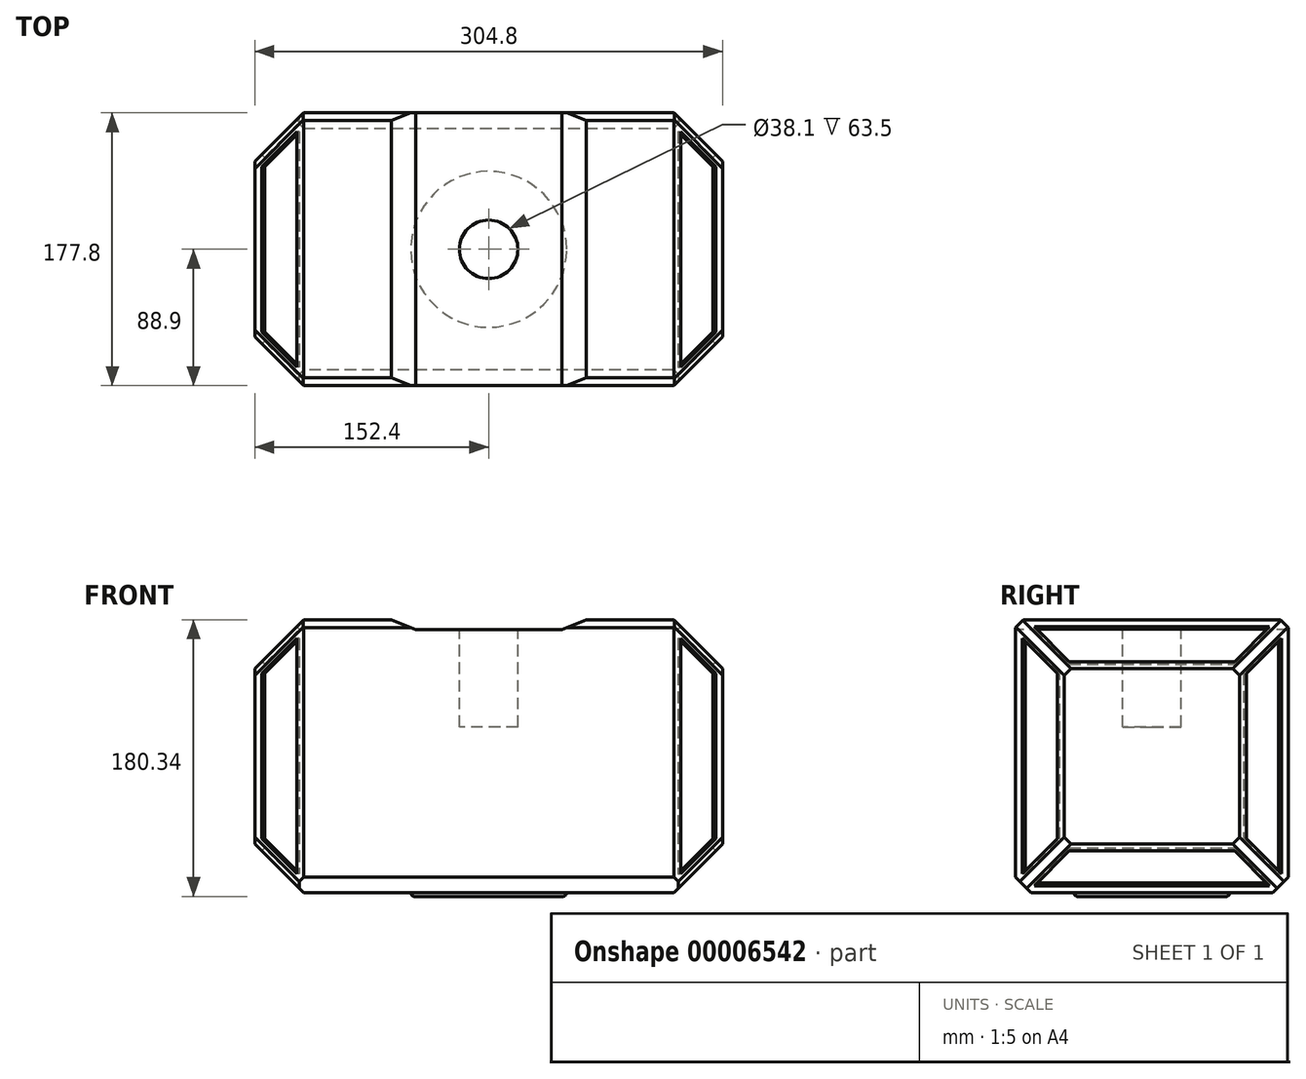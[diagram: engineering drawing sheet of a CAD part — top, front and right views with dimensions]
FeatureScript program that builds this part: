
annotation { "Feature Type Name" : "Feature", "Feature Type Description" : "" }
export const myFeature = defineFeature(function(context is Context, id is Id, definition is map)
    precondition{}
    {
        {
            var Q0;
            Q0=qCreatedBy(makeId("Top.planeOp"),FACE);
            var sketch = newSketch(context, id + "F0", { "sketchPlane" : qUnion([Q0])});
            skLineSegment(sketch, "E0.bottom", {"start": v(-152.4, -88.9) * mm, "end": v(152.4, -88.9) * mm});
            skLineSegment(sketch, "E0.top", {"start": v(-152.4, 88.9) * mm, "end": v(152.4, 88.9) * mm});
            skLineSegment(sketch, "E0.left", {"start": v(-152.4, -88.9) * mm, "end": v(-152.4, 88.9) * mm});
            skLineSegment(sketch, "E0.right", {"start": v(152.4, -88.9) * mm, "end": v(152.4, 88.9) * mm});
            skSolve(sketch);
        }
        {
            var Q0;
            Q0=makeQuery(id+"F0.imprint","IMPRINT",FACE,{"disambiguationData":[TD([[makeQuery(id+"F0.imprint","IMPRINT",EDGE,{"derivedFrom":sQuery(id+"F0.wireOp",EDGE,"E0.bottom")}),1.0]])]});
            extrude(context, id + "F1", {"entities" : qUnion([Q0]), "depth" : 177.8 * mm});
        }
        {
            var Q0;
            Q0=makeQuery(id+"F1.opExtrude","SWEPT_EDGE",EDGE,{"disambiguationData":[OSD([sQuery(id+"F0.wireOp",EDGE,"E0.bottom"),sQuery(id+"F0.wireOp",EDGE,"E0.left")])]});
            var Q1;
            Q1=makeQuery(id+"F1.opExtrude","CAP_EDGE",EDGE,{"disambiguationData":[OSD([sQuery(id+"F0.wireOp",EDGE,"E0.left")])],"isStart":false});
            var Q2;
            Q2=makeQuery(id+"F1.opExtrude","CAP_EDGE",EDGE,{"disambiguationData":[OSD([sQuery(id+"F0.wireOp",EDGE,"E0.left")])],"isStart":true});
            var Q3;
            Q3=makeQuery(id+"F1.opExtrude","SWEPT_EDGE",EDGE,{"disambiguationData":[OSD([sQuery(id+"F0.wireOp",EDGE,"E0.top"),sQuery(id+"F0.wireOp",EDGE,"E0.left")])]});
            var Q4;
            Q4=makeQuery(id+"F1.opExtrude","SWEPT_EDGE",EDGE,{"disambiguationData":[OSD([sQuery(id+"F0.wireOp",EDGE,"E0.bottom"),sQuery(id+"F0.wireOp",EDGE,"E0.right")])]});
            var Q5;
            Q5=makeQuery(id+"F1.opExtrude","CAP_EDGE",EDGE,{"disambiguationData":[OSD([sQuery(id+"F0.wireOp",EDGE,"E0.right")])],"isStart":false});
            var Q6;
            Q6=makeQuery(id+"F1.opExtrude","SWEPT_EDGE",EDGE,{"disambiguationData":[OSD([sQuery(id+"F0.wireOp",EDGE,"E0.top"),sQuery(id+"F0.wireOp",EDGE,"E0.right")])]});
            var Q7;
            Q7=makeQuery(id+"F1.opExtrude","CAP_EDGE",EDGE,{"disambiguationData":[OSD([sQuery(id+"F0.wireOp",EDGE,"E0.right")])],"isStart":true});
            chamfer(context, id + "F2", {"entities" : qUnion([Q0, Q1, Q2, Q3, Q4, Q5, Q6, Q7]), "width" : 31.75 * mm, "tangentPropagation" : true});
        }
        {
            var Q0;
            Q0=makeQuery(id+"F1.opExtrude","CAP_FACE",FACE,{"disambiguationData":[OSD([sQuery(id+"F0.wireOp",EDGE,"E0.bottom"),sQuery(id+"F0.wireOp",EDGE,"E0.top"),sQuery(id+"F0.wireOp",EDGE,"E0.left"),sQuery(id+"F0.wireOp",EDGE,"E0.right")])],"isStart":true});
            var sketch = newSketch(context, id + "F3", { "sketchPlane" : qUnion([Q0])});
            skCircle(sketch, "E1", {"center": v(0, 0) * mm, "radius": 50.8 * mm});
            skSolve(sketch);
        }
        {
            var Q0;
            Q0=makeQuery(id+"F3.imprint","IMPRINT",FACE,{"disambiguationData":[TD([[makeQuery(id+"F3.imprint","IMPRINT",EDGE,{"derivedFrom":sQuery(id+"F3.wireOp",EDGE,"E1")}),1.0]])]});
            extrude(context, id + "F4", {"entities" : qUnion([Q0]), "operationType" : NewBodyOperationType.ADD, "depth" : 2.54 * mm});
        }
        {
            var Q0;
            Q0=makeQuery(id+"F4.opExtrude","CAP_EDGE",EDGE,{"disambiguationData":[OSD([sQuery(id+"F3.wireOp",EDGE,"E1")])],"isStart":false});
            fillet(context, id + "F5", {"entities" : qUnion([Q0]), "radius" : 2.54 * mm, "tangentPropagation" : true, "allowEdgeOverflow" : false});
        }
        {
            var Q0;
            {var subQ0=sQuery(id+"F0.wireOp",EDGE,"E0.right");Q0=makeQuery(id+"F2.opChamfer","BLEND_FACE",FACE,{"disambiguationData":[OSD([subQ0]),TDD([makeQuery(id+"F1.opExtrude","CAP_EDGE",EDGE,{"disambiguationData":[OSD([subQ0])],"isStart":false})])]});}
            var sketch = newSketch(context, id + "F6", { "sketchPlane" : qUnion([Q0])});
            skLineSegment(sketch, "E2.0", {"start": v(53.86, 1.86) * mm, "end": v(76.63, 34.06) * mm});
            skLineSegment(sketch, "E2.1", {"start": v(53.86, 1.86) * mm, "end": v(-53.86, 1.86) * mm});
            skLineSegment(sketch, "E2.2", {"start": v(-76.63, 34.06) * mm, "end": v(-53.86, 1.86) * mm});
            skLineSegment(sketch, "E2.3", {"start": v(-76.63, 34.06) * mm, "end": v(76.63, 34.06) * mm});
            skSolve(sketch);
        }
        {
            var Q0;
            Q0=makeQuery(id+"F6.imprint","IMPRINT",FACE,{"disambiguationData":[TD([[makeQuery(id+"F6.imprint","IMPRINT",EDGE,{"derivedFrom":sQuery(id+"F6.wireOp",EDGE,"E2.0")}),1.0]])]});
            extrude(context, id + "F7", {"entities" : qUnion([Q0]), "operationType" : NewBodyOperationType.REMOVE, "oppositeDirection" : true, "depth" : 2.54 * mm});
        }
        {
            var Q0;
            Q0=qCreatedBy(makeId("Front.planeOp"),FACE);
            var sketch = newSketch(context, id + "F8", { "sketchPlane" : qUnion([Q0])});
            skLineSegment(sketch, "E3", {"start": v(0, 88.9) * mm, "end": v(232.88, 88.9) * mm});
            skSolve(sketch);
        }
        {
            var Q0;
            Q0=makeQuery(id+"F7.boolean.opBoolean","COPY",FACE,{"derivedFrom":makeQuery(id+"F7.opExtrude","CAP_FACE",FACE,{"disambiguationData":[OSD([sQuery(id+"F6.wireOp",EDGE,"E2.0"),sQuery(id+"F6.wireOp",EDGE,"E2.1"),sQuery(id+"F6.wireOp",EDGE,"E2.2"),sQuery(id+"F6.wireOp",EDGE,"E2.3")])],"isStart":false})});
            var Q1;
            Q1=makeQuery(id+"F7.boolean.opBoolean","COPY",FACE,{"derivedFrom":makeQuery(id+"F7.opExtrude","SWEPT_FACE",FACE,{"disambiguationData":[OSD([sQuery(id+"F6.wireOp",EDGE,"E2.0")])]})});
            var Q2;
            Q2=makeQuery(id+"F7.boolean.opBoolean","COPY",FACE,{"derivedFrom":makeQuery(id+"F7.opExtrude","SWEPT_FACE",FACE,{"disambiguationData":[OSD([sQuery(id+"F6.wireOp",EDGE,"E2.3")])]})});
            var Q3;
            Q3=makeQuery(id+"F7.boolean.opBoolean","COPY",FACE,{"derivedFrom":makeQuery(id+"F7.opExtrude","SWEPT_FACE",FACE,{"disambiguationData":[OSD([sQuery(id+"F6.wireOp",EDGE,"E2.1")])]})});
            var Q4;
            Q4=makeQuery(id+"F7.boolean.opBoolean","COPY",FACE,{"derivedFrom":makeQuery(id+"F7.opExtrude","SWEPT_FACE",FACE,{"disambiguationData":[OSD([sQuery(id+"F6.wireOp",EDGE,"E2.2")])]})});
            var Q5;
            Q5=sQuery(id+"F8.wireOp",EDGE,"E3");
            circularPattern(context, id + "F9", {"faces" : qUnion([Q0, Q1, Q2, Q3, Q4]), "axis" : qUnion([Q5]), "angle" : 90 * degree, "instanceCount" : 4, "patternType" : PatternType.FACE});
        }
        {
            var Q0;
            {var subQ0=sQuery(id+"F0.wireOp",EDGE,"E0.left");Q0=makeQuery(id+"F2.opChamfer","BLEND_FACE",FACE,{"disambiguationData":[OSD([subQ0]),TDD([makeQuery(id+"F1.opExtrude","CAP_EDGE",EDGE,{"disambiguationData":[OSD([subQ0])],"isStart":true})])]});}
            var sketch = newSketch(context, id + "F10", { "sketchPlane" : qUnion([Q0])});
            skLineSegment(sketch, "E4.0", {"start": v(53.86, 123.86) * mm, "end": v(76.63, 91.66) * mm});
            skLineSegment(sketch, "E4.1", {"start": v(-53.86, 123.86) * mm, "end": v(53.86, 123.86) * mm});
            skLineSegment(sketch, "E4.2", {"start": v(-76.63, 91.66) * mm, "end": v(-53.86, 123.86) * mm});
            skLineSegment(sketch, "E4.3", {"start": v(76.63, 91.66) * mm, "end": v(-76.63, 91.66) * mm});
            skSolve(sketch);
        }
        {
            var Q0;
            Q0=makeQuery(id+"F10.imprint","IMPRINT",FACE,{"disambiguationData":[TD([[makeQuery(id+"F10.imprint","IMPRINT",EDGE,{"derivedFrom":sQuery(id+"F10.wireOp",EDGE,"E4.0")}),-1.0]])]});
            extrude(context, id + "F11", {"entities" : qUnion([Q0]), "operationType" : NewBodyOperationType.REMOVE, "oppositeDirection" : true, "depth" : 2.54 * mm});
        }
        {
            var Q0;
            Q0=qCreatedBy(makeId("Front.planeOp"),FACE);
            var sketch = newSketch(context, id + "F12", { "sketchPlane" : qUnion([Q0])});
            skLineSegment(sketch, "E5", {"start": v(0, 88.9) * mm, "end": v(227.16, 88.9) * mm});
            skSolve(sketch);
        }
        {
            var Q0;
            Q0=makeQuery(id+"F11.boolean.opBoolean","COPY",FACE,{"derivedFrom":makeQuery(id+"F11.opExtrude","SWEPT_FACE",FACE,{"disambiguationData":[OSD([sQuery(id+"F10.wireOp",EDGE,"E4.3")])]})});
            var Q1;
            Q1=makeQuery(id+"F11.boolean.opBoolean","COPY",FACE,{"derivedFrom":makeQuery(id+"F11.opExtrude","SWEPT_FACE",FACE,{"disambiguationData":[OSD([sQuery(id+"F10.wireOp",EDGE,"E4.2")])]})});
            var Q2;
            Q2=makeQuery(id+"F11.boolean.opBoolean","COPY",FACE,{"derivedFrom":makeQuery(id+"F11.opExtrude","SWEPT_FACE",FACE,{"disambiguationData":[OSD([sQuery(id+"F10.wireOp",EDGE,"E4.0")])]})});
            var Q3;
            Q3=makeQuery(id+"F11.boolean.opBoolean","COPY",FACE,{"derivedFrom":makeQuery(id+"F11.opExtrude","SWEPT_FACE",FACE,{"disambiguationData":[OSD([sQuery(id+"F10.wireOp",EDGE,"E4.1")])]})});
            var Q4;
            Q4=makeQuery(id+"F11.boolean.opBoolean","COPY",FACE,{"derivedFrom":makeQuery(id+"F11.opExtrude","CAP_FACE",FACE,{"disambiguationData":[OSD([sQuery(id+"F10.wireOp",EDGE,"E4.0"),sQuery(id+"F10.wireOp",EDGE,"E4.1"),sQuery(id+"F10.wireOp",EDGE,"E4.2"),sQuery(id+"F10.wireOp",EDGE,"E4.3")])],"isStart":false})});
            var Q5;
            Q5=sQuery(id+"F12.wireOp",EDGE,"E5");
            circularPattern(context, id + "F13", {"faces" : qUnion([Q0, Q1, Q2, Q3, Q4]), "axis" : qUnion([Q5]), "angle" : 90 * degree, "instanceCount" : 4, "patternType" : PatternType.FACE});
        }
        {
            var Q0;
            Q0=makeQuery(id+"F1.opExtrude","SWEPT_FACE",FACE,{"disambiguationData":[OSD([sQuery(id+"F0.wireOp",EDGE,"E0.bottom")])]});
            var sketch = newSketch(context, id + "F14", { "sketchPlane" : qUnion([Q0])});
            skLineSegment(sketch, "E6", {"start": v(0, 177.8) * mm, "end": v(0, -20.13) * mm});
            skLineSegment(sketch, "E7", {"start": v(0, 171.45) * mm, "end": v(47.7, 171.45) * mm});
            skLineSegment(sketch, "E8", {"start": v(47.7, 171.45) * mm, "end": v(63.5, 177.8) * mm});
            skLineSegment(sketch, "E9.0.MirrorCS", {"start": v(0, 171.45) * mm, "end": v(-47.7, 171.45) * mm});
            skLineSegment(sketch, "E10.0.MirrorCS", {"start": v(-47.7, 171.45) * mm, "end": v(-63.5, 177.8) * mm});
            skSolve(sketch);
        }
        {
            var Q0;
            {var subQ4=sQuery(id+"F14.wireOp",EDGE,"E9.0.MirrorCS");Q0=makeQuery(id+"F14.imprint","IMPRINT",FACE,{"disambiguationData":[TD([[makeQuery(id+"F14.imprint","IMPRINT",EDGE,{"derivedFrom":subQ4}),-1.0]])]});}
            var Q1;
            {var subQ4=sQuery(id+"F14.wireOp",EDGE,"E7");Q1=makeQuery(id+"F14.imprint","IMPRINT",FACE,{"disambiguationData":[TD([[makeQuery(id+"F14.imprint","IMPRINT",EDGE,{"derivedFrom":subQ4}),1.0]])]});}
            extrude(context, id + "F15", {"entities" : qUnion([Q0, Q1]), "operationType" : NewBodyOperationType.REMOVE, "oppositeDirection" : true, "depth" : 177.8 * mm});
        }
        {
            var Q0;
            Q0=makeQuery(id+"F1.opExtrude","CAP_EDGE",EDGE,{"disambiguationData":[OSD([sQuery(id+"F0.wireOp",EDGE,"E0.bottom")])],"isStart":true});
            var Q1;
            Q1=makeQuery(id+"F1.opExtrude","CAP_EDGE",EDGE,{"disambiguationData":[OSD([sQuery(id+"F0.wireOp",EDGE,"E0.top")])],"isStart":true});
            chamfer(context, id + "F16", {"entities" : qUnion([Q0, Q1]), "width" : 10.16 * mm, "tangentPropagation" : true});
        }
        {
            var Q0;
            {var subQ0=sQuery(id+"F0.wireOp",EDGE,"E0.left");Q0=makeQuery(id+"F2.opChamfer","BLEND_EDGE",EDGE,{"blendedFrom":[makeQuery(id+"F1.opExtrude","SWEPT_EDGE",EDGE,{"disambiguationData":[OSD([sQuery(id+"F0.wireOp",EDGE,"E0.bottom"),subQ0])]}),makeQuery(id+"F1.opExtrude","CAP_EDGE",EDGE,{"disambiguationData":[OSD([subQ0])],"isStart":true})],"blendedInto":[]});}
            var Q1;
            {var subQ0=sQuery(id+"F0.wireOp",EDGE,"E0.left");Q1=makeQuery(id+"F2.opChamfer","BLEND_EDGE",EDGE,{"blendedFrom":[makeQuery(id+"F1.opExtrude","SWEPT_EDGE",EDGE,{"disambiguationData":[OSD([sQuery(id+"F0.wireOp",EDGE,"E0.top"),subQ0])]}),makeQuery(id+"F1.opExtrude","CAP_EDGE",EDGE,{"disambiguationData":[OSD([subQ0])],"isStart":true})],"blendedInto":[]});}
            var Q2;
            {var subQ0=sQuery(id+"F0.wireOp",EDGE,"E0.right");Q2=makeQuery(id+"F2.opChamfer","BLEND_EDGE",EDGE,{"blendedFrom":[makeQuery(id+"F1.opExtrude","SWEPT_EDGE",EDGE,{"disambiguationData":[OSD([sQuery(id+"F0.wireOp",EDGE,"E0.top"),subQ0])]}),makeQuery(id+"F1.opExtrude","CAP_EDGE",EDGE,{"disambiguationData":[OSD([subQ0])],"isStart":true})],"blendedInto":[]});}
            var Q3;
            {var subQ0=sQuery(id+"F0.wireOp",EDGE,"E0.right");Q3=makeQuery(id+"F2.opChamfer","BLEND_EDGE",EDGE,{"blendedFrom":[makeQuery(id+"F1.opExtrude","SWEPT_EDGE",EDGE,{"disambiguationData":[OSD([sQuery(id+"F0.wireOp",EDGE,"E0.bottom"),subQ0])]}),makeQuery(id+"F1.opExtrude","CAP_EDGE",EDGE,{"disambiguationData":[OSD([subQ0])],"isStart":true})],"blendedInto":[]});}
            var Q4;
            {var subQ0=sQuery(id+"F0.wireOp",EDGE,"E0.left");Q4=makeQuery(id+"F2.opChamfer","BLEND_EDGE",EDGE,{"blendedFrom":[makeQuery(id+"F1.opExtrude","SWEPT_EDGE",EDGE,{"disambiguationData":[OSD([sQuery(id+"F0.wireOp",EDGE,"E0.top"),subQ0])]}),makeQuery(id+"F1.opExtrude","CAP_EDGE",EDGE,{"disambiguationData":[OSD([subQ0])],"isStart":false})],"blendedInto":[]});}
            var Q5;
            {var subQ0=sQuery(id+"F0.wireOp",EDGE,"E0.left");Q5=makeQuery(id+"F2.opChamfer","BLEND_EDGE",EDGE,{"blendedFrom":[makeQuery(id+"F1.opExtrude","SWEPT_EDGE",EDGE,{"disambiguationData":[OSD([sQuery(id+"F0.wireOp",EDGE,"E0.bottom"),subQ0])]}),makeQuery(id+"F1.opExtrude","CAP_EDGE",EDGE,{"disambiguationData":[OSD([subQ0])],"isStart":false})],"blendedInto":[]});}
            var Q6;
            {var subQ0=sQuery(id+"F0.wireOp",EDGE,"E0.right");Q6=makeQuery(id+"F2.opChamfer","BLEND_EDGE",EDGE,{"blendedFrom":[makeQuery(id+"F1.opExtrude","SWEPT_EDGE",EDGE,{"disambiguationData":[OSD([sQuery(id+"F0.wireOp",EDGE,"E0.bottom"),subQ0])]}),makeQuery(id+"F1.opExtrude","CAP_EDGE",EDGE,{"disambiguationData":[OSD([subQ0])],"isStart":false})],"blendedInto":[]});}
            var Q7;
            {var subQ0=sQuery(id+"F0.wireOp",EDGE,"E0.right");Q7=makeQuery(id+"F2.opChamfer","BLEND_EDGE",EDGE,{"blendedFrom":[makeQuery(id+"F1.opExtrude","SWEPT_EDGE",EDGE,{"disambiguationData":[OSD([sQuery(id+"F0.wireOp",EDGE,"E0.top"),subQ0])]}),makeQuery(id+"F1.opExtrude","CAP_EDGE",EDGE,{"disambiguationData":[OSD([subQ0])],"isStart":false})],"blendedInto":[]});}
            chamfer(context, id + "F17", {"entities" : qUnion([Q0, Q1, Q2, Q3, Q4, Q5, Q6, Q7]), "width" : 6.35 * mm, "tangentPropagation" : true});
        }
        {
            var Q0;
            {var subQ0=sQuery(id+"F0.wireOp",EDGE,"E0.bottom");Q0=makeQuery(id+"F15.boolean.opBoolean","SPLIT",EDGE,{"disambiguationData":[TD([makeQuery(id+"F15.opExtrude","SWEPT_FACE",FACE,{"disambiguationData":[OSD([sQuery(id+"F14.wireOp",EDGE,"E10.0.MirrorCS")])]})])],"derivedFrom":makeQuery(id+"F1.opExtrude","CAP_EDGE",EDGE,{"disambiguationData":[OSD([subQ0])],"isStart":false})});}
            var Q1;
            Q1=makeQuery(id+"F15.boolean.opBoolean","COPY",EDGE,{"derivedFrom":makeQuery(id+"F15.opExtrude","CAP_EDGE",EDGE,{"disambiguationData":[OSD([sQuery(id+"F14.wireOp",EDGE,"E10.0.MirrorCS")])],"isStart":true})});
            var Q2;
            Q2=makeQuery(id+"F15.boolean.opBoolean","COPY",EDGE,{"derivedFrom":makeQuery(id+"F15.opExtrude","CAP_EDGE",EDGE,{"disambiguationData":[OSD([sQuery(id+"F14.wireOp",EDGE,"E7"),sQuery(id+"F14.wireOp",EDGE,"E9.0.MirrorCS")])],"isStart":true})});
            var Q3;
            Q3=makeQuery(id+"F15.boolean.opBoolean","COPY",EDGE,{"derivedFrom":makeQuery(id+"F15.opExtrude","CAP_EDGE",EDGE,{"disambiguationData":[OSD([sQuery(id+"F14.wireOp",EDGE,"E8")])],"isStart":true})});
            var Q4;
            {var subQ0=sQuery(id+"F0.wireOp",EDGE,"E0.bottom");Q4=makeQuery(id+"F15.boolean.opBoolean","SPLIT",EDGE,{"disambiguationData":[TD([makeQuery(id+"F15.opExtrude","SWEPT_FACE",FACE,{"disambiguationData":[OSD([sQuery(id+"F14.wireOp",EDGE,"E8")])]})])],"derivedFrom":makeQuery(id+"F1.opExtrude","CAP_EDGE",EDGE,{"disambiguationData":[OSD([subQ0])],"isStart":false})});}
            var Q5;
            {var subQ0=sQuery(id+"F0.wireOp",EDGE,"E0.top");Q5=makeQuery(id+"F15.boolean.opBoolean","SPLIT",EDGE,{"disambiguationData":[TD([makeQuery(id+"F15.opExtrude","SWEPT_FACE",FACE,{"disambiguationData":[OSD([sQuery(id+"F14.wireOp",EDGE,"E8")])]})])],"derivedFrom":makeQuery(id+"F1.opExtrude","CAP_EDGE",EDGE,{"disambiguationData":[OSD([subQ0])],"isStart":false})});}
            var Q6;
            Q6=makeQuery(id+"F15.boolean.opBoolean","COPY",EDGE,{"derivedFrom":makeQuery(id+"F15.opExtrude","CAP_EDGE",EDGE,{"disambiguationData":[OSD([sQuery(id+"F14.wireOp",EDGE,"E8")])],"isStart":false})});
            var Q7;
            Q7=makeQuery(id+"F15.boolean.opBoolean","COPY",EDGE,{"derivedFrom":makeQuery(id+"F15.opExtrude","CAP_EDGE",EDGE,{"disambiguationData":[OSD([sQuery(id+"F14.wireOp",EDGE,"E7"),sQuery(id+"F14.wireOp",EDGE,"E9.0.MirrorCS")])],"isStart":false})});
            var Q8;
            Q8=makeQuery(id+"F15.boolean.opBoolean","COPY",EDGE,{"derivedFrom":makeQuery(id+"F15.opExtrude","CAP_EDGE",EDGE,{"disambiguationData":[OSD([sQuery(id+"F14.wireOp",EDGE,"E10.0.MirrorCS")])],"isStart":false})});
            var Q9;
            {var subQ0=sQuery(id+"F0.wireOp",EDGE,"E0.top");Q9=makeQuery(id+"F15.boolean.opBoolean","SPLIT",EDGE,{"disambiguationData":[TD([makeQuery(id+"F15.opExtrude","SWEPT_FACE",FACE,{"disambiguationData":[OSD([sQuery(id+"F14.wireOp",EDGE,"E10.0.MirrorCS")])]})])],"derivedFrom":makeQuery(id+"F1.opExtrude","CAP_EDGE",EDGE,{"disambiguationData":[OSD([subQ0])],"isStart":false})});}
            chamfer(context, id + "F18", {"entities" : qUnion([Q0, Q1, Q2, Q3, Q4, Q5, Q6, Q7, Q8, Q9]), "width" : 5.08 * mm, "tangentPropagation" : true});
        }
        {
            var Q0;
            Q0=makeQuery(id+"F15.boolean.opBoolean","COPY",FACE,{"derivedFrom":makeQuery(id+"F15.opExtrude","SWEPT_FACE",FACE,{"disambiguationData":[OSD([sQuery(id+"F14.wireOp",EDGE,"E7"),sQuery(id+"F14.wireOp",EDGE,"E9.0.MirrorCS")])]})});
            var sketch = newSketch(context, id + "F19", { "sketchPlane" : qUnion([Q0])});
            skCircle(sketch, "E11", {"center": v(0, 0) * mm, "radius": 19.05 * mm});
            skSolve(sketch);
        }
        {
            var Q0;
            Q0=makeQuery(id+"F19.imprint","IMPRINT",FACE,{"disambiguationData":[TD([[makeQuery(id+"F19.imprint","IMPRINT",EDGE,{"derivedFrom":sQuery(id+"F19.wireOp",EDGE,"E11")}),1.0]])]});
            extrude(context, id + "F20", {"entities" : qUnion([Q0]), "operationType" : NewBodyOperationType.REMOVE, "oppositeDirection" : true, "depth" : 63.5 * mm});
        }
    });
